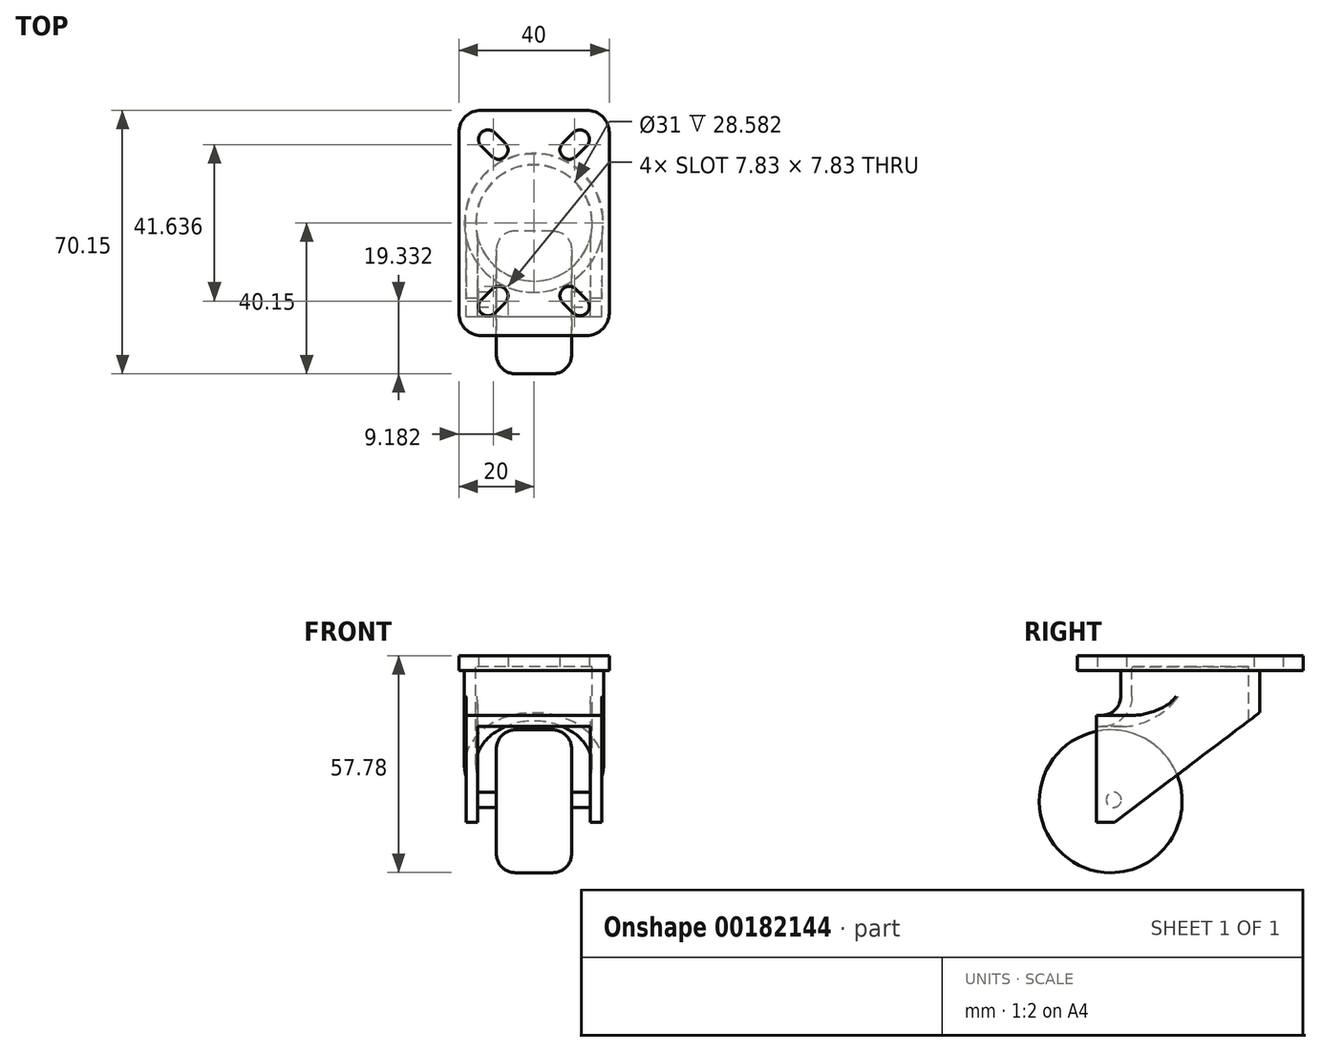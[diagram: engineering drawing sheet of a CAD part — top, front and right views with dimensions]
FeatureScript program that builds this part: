
annotation { "Feature Type Name" : "Feature", "Feature Type Description" : "" }
export const myFeature = defineFeature(function(context is Context, id is Id, definition is map)
    precondition{}
    {
        {
            var Q0;
            Q0=qCreatedBy(makeId("Top.planeOp"),FACE);
            var sketch = newSketch(context, id + "F0", { "sketchPlane" : qUnion([Q0])});
            skLineSegment(sketch, "E0.bottom", {"start": v(14, 30) * mm, "end": v(-14, 30) * mm});
            skLineSegment(sketch, "E0.top", {"start": v(14, -30) * mm, "end": v(-14, -30) * mm});
            skLineSegment(sketch, "E0.left", {"start": v(20, 24) * mm, "end": v(20, -24) * mm});
            skLineSegment(sketch, "E0.right", {"start": v(-20, 24) * mm, "end": v(-20, -24) * mm});
            skPoint(sketch, "E0.middle", {"position": v(0, 0) * mm});
            skPoint(sketch, "E1.visualSharp", {"position": v(-20, 30) * mm});
            skArc(sketch, "E1.filletArc", {"start": v(-14, 30) * mm, "mid": v(-18.24, 28.24) * mm, "end": v(-20, 24) * mm});
            skPoint(sketch, "E2.visualSharp", {"position": v(20, 30) * mm});
            skArc(sketch, "E2.filletArc", {"start": v(20, 24) * mm, "mid": v(18.24, 28.24) * mm, "end": v(14, 30) * mm});
            skPoint(sketch, "E3.visualSharp", {"position": v(-20, -30) * mm});
            skArc(sketch, "E3.filletArc", {"start": v(-20, -24) * mm, "mid": v(-18.24, -28.24) * mm, "end": v(-14, -30) * mm});
            skPoint(sketch, "E4.visualSharp", {"position": v(20, -30) * mm});
            skArc(sketch, "E4.filletArc", {"start": v(14, -30) * mm, "mid": v(18.24, -28.24) * mm, "end": v(20, -24) * mm});
            skLineSegment(sketch, "E5", {"start": v(-14, 24) * mm, "end": v(-14, 24) * mm});
            skLineSegment(sketch, "E6", {"start": v(-14, 20.46) * mm, "end": v(-11.17, 17.64) * mm});
            skLineSegment(sketch, "E7", {"start": v(-10.46, 24) * mm, "end": v(-7.64, 21.17) * mm});
            skLineSegment(sketch, "E8", {"start": v(-7.64, 17.64) * mm, "end": v(-7.64, 17.64) * mm});
            skPoint(sketch, "E9.visualSharp", {"position": v(-15.77, 22.23) * mm});
            skArc(sketch, "E9.filletArc", {"start": v(-14, 24) * mm, "mid": v(-14.73, 22.23) * mm, "end": v(-14, 20.46) * mm});
            skPoint(sketch, "E10.visualSharp", {"position": v(-12.23, 25.77) * mm});
            skArc(sketch, "E10.filletArc", {"start": v(-10.46, 24) * mm, "mid": v(-12.23, 24.73) * mm, "end": v(-14, 24) * mm});
            skPoint(sketch, "E11.visualSharp", {"position": v(-5.87, 19.4) * mm});
            skArc(sketch, "E11.filletArc", {"start": v(-7.64, 17.64) * mm, "mid": v(-6.9, 19.4) * mm, "end": v(-7.64, 21.17) * mm});
            skPoint(sketch, "E12.visualSharp", {"position": v(-9.4, 15.87) * mm});
            skArc(sketch, "E12.filletArc", {"start": v(-11.17, 17.64) * mm, "mid": v(-9.4, 16.9) * mm, "end": v(-7.64, 17.64) * mm});
            skLineSegment(sketch, "E13.MirrorCS", {"start": v(10.46, 24) * mm, "end": v(7.64, 21.17) * mm});
            skArc(sketch, "E14.MirrorCS", {"start": v(7.64, 17.64) * mm, "mid": v(6.9, 19.4) * mm, "end": v(7.64, 21.17) * mm});
            skArc(sketch, "E15.MirrorCS", {"start": v(11.17, 17.64) * mm, "mid": v(9.4, 16.9) * mm, "end": v(7.64, 17.64) * mm});
            skLineSegment(sketch, "E16.MirrorCS", {"start": v(14, 20.46) * mm, "end": v(11.17, 17.64) * mm});
            skArc(sketch, "E17.MirrorCS", {"start": v(14, 24) * mm, "mid": v(14.73, 22.23) * mm, "end": v(14, 20.46) * mm});
            skArc(sketch, "E18.MirrorCS", {"start": v(10.46, 24) * mm, "mid": v(12.23, 24.73) * mm, "end": v(14, 24) * mm});
            skArc(sketch, "E19.MirrorCS", {"start": v(11.17, -17.64) * mm, "mid": v(9.4, -16.9) * mm, "end": v(7.64, -17.64) * mm});
            skArc(sketch, "E20.MirrorCS", {"start": v(7.64, -17.64) * mm, "mid": v(6.9, -19.4) * mm, "end": v(7.64, -21.17) * mm});
            skLineSegment(sketch, "E21.MirrorCS", {"start": v(10.46, -24) * mm, "end": v(7.64, -21.17) * mm});
            skArc(sketch, "E22.MirrorCS", {"start": v(14, -24) * mm, "mid": v(14.73, -22.23) * mm, "end": v(14, -20.46) * mm});
            skArc(sketch, "E23.MirrorCS", {"start": v(10.46, -24) * mm, "mid": v(12.23, -24.73) * mm, "end": v(14, -24) * mm});
            skLineSegment(sketch, "E24.MirrorCS", {"start": v(14, -20.46) * mm, "end": v(11.17, -17.64) * mm});
            skArc(sketch, "E25.MirrorCS", {"start": v(-7.64, -17.64) * mm, "mid": v(-6.9, -19.4) * mm, "end": v(-7.64, -21.17) * mm});
            skArc(sketch, "E26.MirrorCS", {"start": v(-11.17, -17.64) * mm, "mid": v(-9.4, -16.9) * mm, "end": v(-7.64, -17.64) * mm});
            skLineSegment(sketch, "E27.MirrorCS", {"start": v(-14, -20.46) * mm, "end": v(-11.17, -17.64) * mm});
            skArc(sketch, "E28.MirrorCS", {"start": v(-14, -24) * mm, "mid": v(-14.73, -22.23) * mm, "end": v(-14, -20.46) * mm});
            skArc(sketch, "E29.MirrorCS", {"start": v(-10.46, -24) * mm, "mid": v(-12.23, -24.73) * mm, "end": v(-14, -24) * mm});
            skLineSegment(sketch, "E30.MirrorCS", {"start": v(-10.46, -24) * mm, "end": v(-7.64, -21.17) * mm});
            skSolve(sketch);
        }
        {
            var Q0;
            Q0=makeQuery(id+"F0.imprint","IMPRINT",FACE,{"disambiguationData":[TD([[makeQuery(id+"F0.imprint","IMPRINT",EDGE,{"derivedFrom":sQuery(id+"F0.wireOp",EDGE,"E0.bottom")}),1.0]])]});
            extrude(context, id + "F1", {"entities" : qUnion([Q0]), "depth" : 4 * mm});
        }
        {
            var Q0;
            Q0=makeQuery(id+"F1.opExtrude","CAP_FACE",FACE,{"disambiguationData":[OSD([sQuery(id+"F0.wireOp",EDGE,"E0.bottom"),sQuery(id+"F0.wireOp",EDGE,"E0.top"),sQuery(id+"F0.wireOp",EDGE,"E0.left"),sQuery(id+"F0.wireOp",EDGE,"E0.right"),sQuery(id+"F0.wireOp",EDGE,"E1.filletArc"),sQuery(id+"F0.wireOp",EDGE,"E2.filletArc"),sQuery(id+"F0.wireOp",EDGE,"E3.filletArc"),sQuery(id+"F0.wireOp",EDGE,"E4.filletArc"),sQuery(id+"F0.wireOp",EDGE,"E6"),sQuery(id+"F0.wireOp",EDGE,"E7"),sQuery(id+"F0.wireOp",EDGE,"E9.filletArc"),sQuery(id+"F0.wireOp",EDGE,"E10.filletArc"),sQuery(id+"F0.wireOp",EDGE,"E11.filletArc"),sQuery(id+"F0.wireOp",EDGE,"E12.filletArc"),sQuery(id+"F0.wireOp",EDGE,"E13.MirrorCS"),sQuery(id+"F0.wireOp",EDGE,"E14.MirrorCS"),sQuery(id+"F0.wireOp",EDGE,"E15.MirrorCS"),sQuery(id+"F0.wireOp",EDGE,"E16.MirrorCS"),sQuery(id+"F0.wireOp",EDGE,"E17.MirrorCS"),sQuery(id+"F0.wireOp",EDGE,"E18.MirrorCS"),sQuery(id+"F0.wireOp",EDGE,"E19.MirrorCS"),sQuery(id+"F0.wireOp",EDGE,"E20.MirrorCS"),sQuery(id+"F0.wireOp",EDGE,"E22.MirrorCS"),sQuery(id+"F0.wireOp",EDGE,"E23.MirrorCS"),sQuery(id+"F0.wireOp",EDGE,"E21.MirrorCS"),sQuery(id+"F0.wireOp",EDGE,"E24.MirrorCS"),sQuery(id+"F0.wireOp",EDGE,"E25.MirrorCS"),sQuery(id+"F0.wireOp",EDGE,"E26.MirrorCS"),sQuery(id+"F0.wireOp",EDGE,"E27.MirrorCS"),sQuery(id+"F0.wireOp",EDGE,"E28.MirrorCS"),sQuery(id+"F0.wireOp",EDGE,"E29.MirrorCS"),sQuery(id+"F0.wireOp",EDGE,"E30.MirrorCS")])],"isStart":true});
            var sketch = newSketch(context, id + "F2", { "sketchPlane" : qUnion([Q0])});
            skCircle(sketch, "E31", {"center": v(0, 0) * mm, "radius": 18.5 * mm});
            skSolve(sketch);
        }
        {
            var Q0;
            Q0=makeQuery(id+"F2.imprint","IMPRINT",FACE,{"disambiguationData":[TD([[makeQuery(id+"F2.imprint","IMPRINT",EDGE,{"derivedFrom":sQuery(id+"F2.wireOp",EDGE,"E31")}),1.0]])]});
            extrude(context, id + "F3", {"entities" : qUnion([Q0]), "operationType" : NewBodyOperationType.ADD, "depth" : 35 * mm});
        }
        {
            var Q0;
            Q0=qCreatedBy(makeId("Front.planeOp"),FACE);
            var sketch = newSketch(context, id + "F4", { "sketchPlane" : qUnion([Q0])});
            skLineSegment(sketch, "E32.bottom", {"start": v(0, -11.9) * mm, "end": v(-18, -11.9) * mm});
            skLineSegment(sketch, "E32.top", {"start": v(0, -40.4) * mm, "end": v(-18, -40.4) * mm});
            skLineSegment(sketch, "E32.left", {"start": v(0, -11.9) * mm, "end": v(0, -40.4) * mm});
            skLineSegment(sketch, "E32.right", {"start": v(-18, -11.9) * mm, "end": v(-18, -40.4) * mm});
            skLineSegment(sketch, "E33.MirrorCS", {"start": v(0, -11.9) * mm, "end": v(18, -11.9) * mm});
            skLineSegment(sketch, "E34.MirrorCS", {"start": v(18, -11.9) * mm, "end": v(18, -40.4) * mm});
            skLineSegment(sketch, "E35.MirrorCS", {"start": v(0, -40.4) * mm, "end": v(18, -40.4) * mm});
            skSolve(sketch);
        }
        {
            var Q0;
            Q0=makeQuery(id+"F4.imprint","IMPRINT",FACE,{"disambiguationData":[TD([[makeQuery(id+"F4.imprint","IMPRINT",EDGE,{"derivedFrom":sQuery(id+"F4.wireOp",EDGE,"E32.bottom")}),1.0]])]});
            var Q1;
            Q1=makeQuery(id+"F4.imprint","IMPRINT",FACE,{"disambiguationData":[TD([[makeQuery(id+"F4.imprint","IMPRINT",EDGE,{"derivedFrom":sQuery(id+"F4.wireOp",EDGE,"E32.left")}),1.0]])]});
            extrude(context, id + "F5", {"entities" : qUnion([Q0, Q1]), "operationType" : NewBodyOperationType.ADD, "depth" : 25 * mm});
        }
        {
            var Q0;
            Q0=makeQuery(id+"F5.boolean.opBoolean","INTERSECT",EDGE,{"derivedFrom":[makeQuery(id+"F3.opExtrude","SWEPT_FACE",FACE,{"disambiguationData":[OSD([sQuery(id+"F2.wireOp",EDGE,"E31")])]}),makeQuery(id+"F5.opExtrude","SWEPT_FACE",FACE,{"disambiguationData":[OSD([sQuery(id+"F4.wireOp",EDGE,"E32.bottom"),sQuery(id+"F4.wireOp",EDGE,"E33.MirrorCS")])]})]});
            fillet(context, id + "F6", {"entities" : qUnion([Q0]), "radius" : 5 * mm, "tangentPropagation" : true, "allowEdgeOverflow" : false});
        }
        {
            var Q0;
            Q0=makeQuery(id+"F5.boolean.opBoolean","INTERSECT",EDGE,{"derivedFrom":[makeQuery(id+"F3.opExtrude","SWEPT_FACE",FACE,{"disambiguationData":[OSD([sQuery(id+"F2.wireOp",EDGE,"E31")])]}),makeQuery(id+"F5.opExtrude","SWEPT_FACE",FACE,{"disambiguationData":[OSD([sQuery(id+"F4.wireOp",EDGE,"E32.right")])]})]});
            fillet(context, id + "F7", {"entities" : qUnion([Q0]), "radius" : 5 * mm, "tangentPropagation" : true, "allowEdgeOverflow" : false});
        }
        {
            var Q0;
            Q0=makeQuery(id+"F5.boolean.opBoolean","INTERSECT",EDGE,{"derivedFrom":[makeQuery(id+"F3.opExtrude","SWEPT_FACE",FACE,{"disambiguationData":[OSD([sQuery(id+"F2.wireOp",EDGE,"E31")])]}),makeQuery(id+"F5.opExtrude","SWEPT_FACE",FACE,{"disambiguationData":[OSD([sQuery(id+"F4.wireOp",EDGE,"E34.MirrorCS")])]})]});
            fillet(context, id + "F8", {"entities" : qUnion([Q0]), "radius" : 5 * mm, "tangentPropagation" : true, "allowEdgeOverflow" : false});
        }
        {
            var Q0;
            Q0=qCreatedBy(makeId("Right.planeOp"),FACE);
            var sketch = newSketch(context, id + "F9", { "sketchPlane" : qUnion([Q0])});
            skLineSegment(sketch, "E36", {"start": v(19.85, -10.11) * mm, "end": v(-23.19, -42.76) * mm});
            skLineSegment(sketch, "E37", {"start": v(-23.19, -42.76) * mm, "end": v(19.85, -42.76) * mm});
            skLineSegment(sketch, "E38", {"start": v(19.85, -42.76) * mm, "end": v(19.85, -10.11) * mm});
            skSolve(sketch);
        }
        {
            var Q0;
            Q0 = qSketchRegion(id + "F9", true);
            extrude(context, id + "F10", {"entities" : qUnion([Q0]), "operationType" : NewBodyOperationType.REMOVE, "oppositeDirection" : true, "depth" : 25 * mm, "hasSecondDirection" : true, "secondDirectionOppositeDirection" : false, "secondDirectionDepth" : 25 * mm});
        }
        {
            var Q0;
            Q0=makeQuery(id+"F10.boolean.opBoolean","COPY",FACE,{"derivedFrom":makeQuery(id+"F10.opExtrude","SWEPT_FACE",FACE,{"disambiguationData":[OSD([sQuery(id+"F9.wireOp",EDGE,"E36")])]})});
            var Q1;
            Q1=makeQuery(id+"F5.opExtrude","SWEPT_FACE",FACE,{"disambiguationData":[OSD([sQuery(id+"F4.wireOp",EDGE,"E32.top"),sQuery(id+"F4.wireOp",EDGE,"E35.MirrorCS")])]});
            var Q2;
            Q2=makeQuery(id+"F5.opExtrude","CAP_FACE",FACE,{"disambiguationData":[OSD([sQuery(id+"F4.wireOp",EDGE,"E32.bottom"),sQuery(id+"F4.wireOp",EDGE,"E32.top"),sQuery(id+"F4.wireOp",EDGE,"E32.right"),sQuery(id+"F4.wireOp",EDGE,"E33.MirrorCS"),sQuery(id+"F4.wireOp",EDGE,"E34.MirrorCS"),sQuery(id+"F4.wireOp",EDGE,"E35.MirrorCS")])],"isStart":false});
            shell(context, id + "F11", {"entities" : qUnion([Q0, Q1, Q2]), "thickness" : 3 * mm});
        }
        {
            var Q0;
            Q0=makeQuery(id+"F5.opExtrude","SWEPT_FACE",FACE,{"disambiguationData":[OSD([sQuery(id+"F4.wireOp",EDGE,"E34.MirrorCS")])]});
            var sketch = newSketch(context, id + "F12", { "sketchPlane" : qUnion([Q0])});
            skCircle(sketch, "E39", {"center": v(-20.35, -34.4) * mm, "radius": 2 * mm});
            skSolve(sketch);
        }
        {
            var Q0;
            Q0=makeQuery(id+"F12.imprint","IMPRINT",FACE,{"disambiguationData":[TD([[makeQuery(id+"F12.imprint","IMPRINT",EDGE,{"derivedFrom":sQuery(id+"F12.wireOp",EDGE,"E39")}),1.0]])]});
            var Q1;
            Q1=makeQuery(id+"F5.opExtrude","SWEPT_FACE",FACE,{"disambiguationData":[OSD([sQuery(id+"F4.wireOp",EDGE,"E32.right")])]});
            extrude(context, id + "F13", {"entities" : qUnion([Q0]), "operationType" : NewBodyOperationType.ADD, "endBound" : BoundingType.UP_TO_SURFACE, "oppositeDirection" : true, "endBoundEntityFace" : qUnion([Q1]), "depth" : 25 * mm});
        }
        {
            var Q0;
            Q0=qCreatedBy(makeId("Right.planeOp"),FACE);
            var sketch = newSketch(context, id + "F14", { "sketchPlane" : qUnion([Q0])});
            skCircle(sketch, "E40", {"center": v(-21.15, -34.78) * mm, "radius": 19 * mm});
            skSolve(sketch);
        }
        {
            var Q0;
            Q0=makeQuery(id+"F14.imprint","IMPRINT",FACE,{"disambiguationData":[TD([[makeQuery(id+"F14.imprint","IMPRINT",EDGE,{"derivedFrom":sQuery(id+"F14.wireOp",EDGE,"E40")}),1.0]])]});
            extrude(context, id + "F15", {"entities" : qUnion([Q0]), "operationType" : NewBodyOperationType.ADD, "depth" : 10 * mm, "hasSecondDirection" : true, "secondDirectionOppositeDirection" : true, "secondDirectionDepth" : 10 * mm});
        }
        {
            var Q0;
            Q0=makeQuery(id+"F15.opExtrude","CAP_EDGE",EDGE,{"disambiguationData":[OSD([sQuery(id+"F14.wireOp",EDGE,"E40")])],"isStart":false});
            var Q1;
            Q1=makeQuery(id+"F15.opExtrude","CAP_EDGE",EDGE,{"disambiguationData":[OSD([sQuery(id+"F14.wireOp",EDGE,"E40")])],"isStart":true});
            fillet(context, id + "F16", {"entities" : qUnion([Q0, Q1]), "radius" : 5 * mm, "tangentPropagation" : true, "allowEdgeOverflow" : false});
        }
    });
